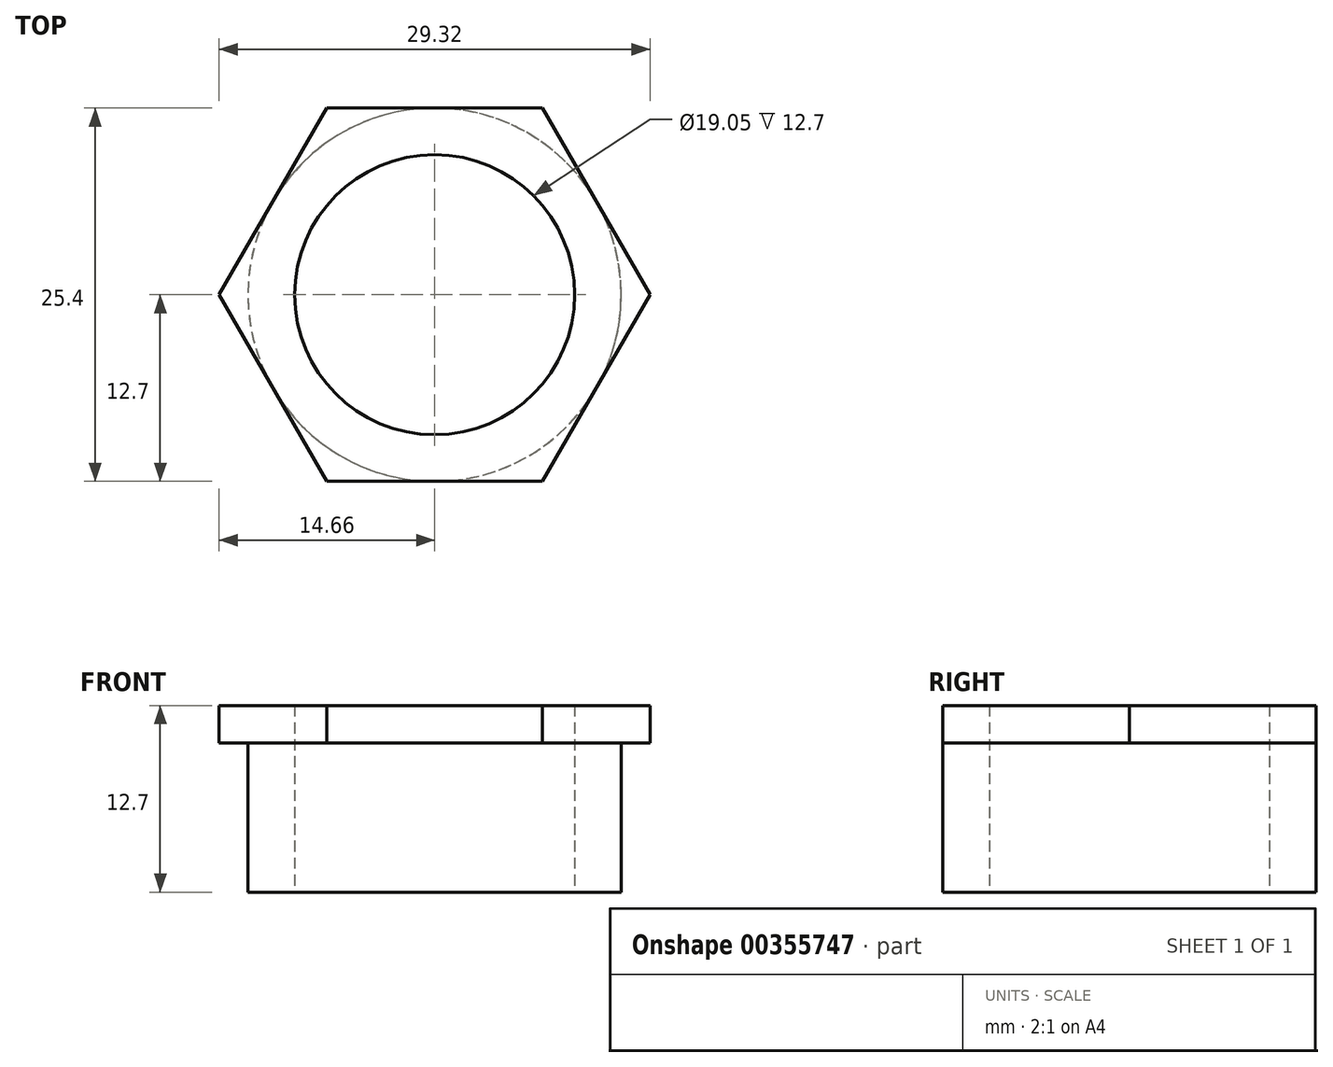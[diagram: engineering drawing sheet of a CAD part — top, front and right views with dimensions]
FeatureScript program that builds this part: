
annotation { "Feature Type Name" : "Feature", "Feature Type Description" : "" }
export const myFeature = defineFeature(function(context is Context, id is Id, definition is map)
    precondition{}
    {
        {
            var Q0;
            Q0=qCreatedBy(makeId("Top.planeOp"),FACE);
            var sketch = newSketch(context, id + "F0", { "sketchPlane" : qUnion([Q0])});
            skCircle(sketch, "E0", {"center": v(0, 0) * mm, "radius": 12.7 * mm});
            skCircle(sketch, "E1", {"center": v(0, 0) * mm, "radius": 9.53 * mm});
            skSolve(sketch);
        }
        {
            var Q0;
            Q0 = qSketchRegion(id + "F0", true);
            extrude(context, id + "F1", {"entities" : qUnion([Q0]), "depth" : 12.7 * mm});
        }
        {
            var Q0;
            Q0=makeQuery(id+"F1.opExtrude","CAP_FACE",FACE,{"disambiguationData":[OSD([sQuery(id+"F0.wireOp",EDGE,"E0"),sQuery(id+"F0.wireOp",EDGE,"E1")])],"isStart":false});
            var sketch = newSketch(context, id + "F2", { "sketchPlane" : qUnion([Q0])});
            skCircle(sketch, "E2.cCircle", {"center": v(0, 0) * mm, "radius": 12.7 * mm, "construction": true});
            skLineSegment(sketch, "E2.0", {"start": v(-7.33, 12.7) * mm, "end": v(7.33, 12.7) * mm});
            skLineSegment(sketch, "E2.1", {"start": v(7.33, 12.7) * mm, "end": v(14.66, 0) * mm});
            skLineSegment(sketch, "E2.2", {"start": v(14.66, 0) * mm, "end": v(7.33, -12.7) * mm});
            skLineSegment(sketch, "E2.3", {"start": v(7.33, -12.7) * mm, "end": v(-7.33, -12.7) * mm});
            skLineSegment(sketch, "E2.4", {"start": v(-7.33, -12.7) * mm, "end": v(-14.66, 0) * mm});
            skLineSegment(sketch, "E2.5", {"start": v(-14.66, 0) * mm, "end": v(-7.33, 12.7) * mm});
            skPoint(sketch, "E2.0.midPoint", {"position": v(0, 12.7) * mm});
            skCircle(sketch, "E3", {"center": v(0, 0) * mm, "radius": 9.53 * mm});
            skSolve(sketch);
        }
        {
            var Q0;
            Q0 = qSketchRegion(id + "F2", true);
            var Q1;
            Q1 = qConstructionFilter(qBodyType(qCreatedBy(id + "F2" ,EDGE), BodyType.WIRE), ConstructionObject.NO);
            extrude(context, id + "F3", {"entities" : qUnion([Q0]), "operationType" : NewBodyOperationType.ADD, "surfaceEntities" : qUnion([Q1]), "oppositeDirection" : true, "depth" : 2.54 * mm});
        }
    });
